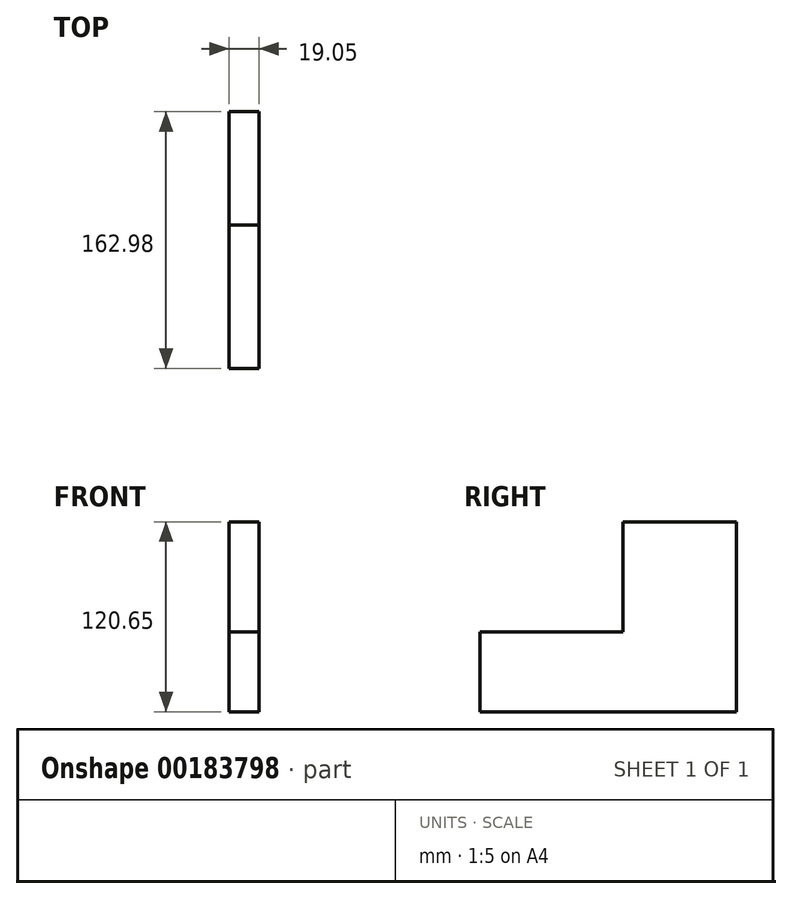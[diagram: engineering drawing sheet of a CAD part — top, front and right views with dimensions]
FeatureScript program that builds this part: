
annotation { "Feature Type Name" : "Feature", "Feature Type Description" : "" }
export const myFeature = defineFeature(function(context is Context, id is Id, definition is map)
    precondition{}
    {
        {
            var Q0;
            Q0=qCreatedBy(makeId("Right.planeOp"),FACE);
            var sketch = newSketch(context, id + "F0", { "sketchPlane" : qUnion([Q0])});
            skLineSegment(sketch, "E0.bottom", {"start": v(0, 0) * mm, "end": v(273.05, 0) * mm});
            skLineSegment(sketch, "E0.top", {"start": v(0, 228.6) * mm, "end": v(273.05, 228.6) * mm});
            skLineSegment(sketch, "E0.left", {"start": v(0, 0) * mm, "end": v(0, 228.6) * mm});
            skLineSegment(sketch, "E0.right", {"start": v(273.05, 0) * mm, "end": v(273.05, 228.6) * mm});
            skSolve(sketch);
        }
        {
            var Q0;
            Q0=qSketchRegion(id+"F0",true);
            extrude(context, id + "F1", {"entities" : qUnion([Q0]), "oppositeDirection" : true, "depth" : 19.05 * mm});
        }
        {
            var Q0;
            Q0=makeQuery(id+"F1.opExtrude","CAP_FACE",FACE,{"disambiguationData":[OSD([sQuery(id+"F0.wireOp",EDGE,"E0.bottom"),sQuery(id+"F0.wireOp",EDGE,"E0.top"),sQuery(id+"F0.wireOp",EDGE,"E0.left"),sQuery(id+"F0.wireOp",EDGE,"E0.right")])],"isStart":true});
            var sketch = newSketch(context, id + "F2", { "sketchPlane" : qUnion([Q0])});
            skLineSegment(sketch, "E1", {"start": v(91.02, 228.6) * mm, "end": v(91.02, 69.85) * mm, "construction": true});
            skLineSegment(sketch, "E2", {"start": v(182.03, 228.6) * mm, "end": v(182.03, 139.7) * mm, "construction": true});
            skLineSegment(sketch, "E3", {"start": v(0, 190.24) * mm, "end": v(91.02, 190.24) * mm, "construction": true});
            skLineSegment(sketch, "E4", {"start": v(91.02, 190.24) * mm, "end": v(182.03, 190.24) * mm, "construction": true});
            skLineSegment(sketch, "E5", {"start": v(182.03, 190.24) * mm, "end": v(273.05, 190.24) * mm, "construction": true});
            skLineSegment(sketch, "E6", {"start": v(273.05, 139.7) * mm, "end": v(182.03, 139.7) * mm});
            skLineSegment(sketch, "E7", {"start": v(273.05, 69.85) * mm, "end": v(91.02, 69.85) * mm});
            skLineSegment(sketch, "E8", {"start": v(40.37, 139.7) * mm, "end": v(40.37, 69.85) * mm, "construction": true});
            skLineSegment(sketch, "E9", {"start": v(40.37, 69.85) * mm, "end": v(40.37, 0) * mm, "construction": true});
            skLineSegment(sketch, "E10", {"start": v(91.02, 69.85) * mm, "end": v(91.02, 0) * mm});
            skLineSegment(sketch, "E11", {"start": v(91.02, 69.85) * mm, "end": v(0, 69.85) * mm, "construction": true});
            skLineSegment(sketch, "E12", {"start": v(182.03, 139.7) * mm, "end": v(182.03, 0) * mm});
            skLineSegment(sketch, "E13", {"start": v(182.03, 139.7) * mm, "end": v(0, 139.7) * mm, "construction": true});
            skSolve(sketch);
        }
        {
            var Q0;
            {var subQ1=sQuery(id+"F2.wireOp",EDGE,"E6");Q0=makeQuery(id+"F2.imprint","IMPRINT",FACE,{"disambiguationData":[TD([[makeQuery(id+"F2.imprint","IMPRINT",EDGE,{"derivedFrom":subQ1}),-1.0]])]});}
            var Q1;
            Q1=makeQuery(id+"F1.opExtrude","CAP_FACE",FACE,{"disambiguationData":[OSD([sQuery(id+"F0.wireOp",EDGE,"E0.bottom"),sQuery(id+"F0.wireOp",EDGE,"E0.top"),sQuery(id+"F0.wireOp",EDGE,"E0.left"),sQuery(id+"F0.wireOp",EDGE,"E0.right")])],"isStart":false});
            extrude(context, id + "F3", {"entities" : qUnion([Q0]), "operationType" : NewBodyOperationType.REMOVE, "endBound" : BoundingType.UP_TO_SURFACE, "oppositeDirection" : true, "endBoundEntityFace" : qUnion([Q1]), "depth" : 25.4 * mm});
        }
        {
            var Q0;
            Q0=makeQuery(id+"F1.opExtrude","CAP_FACE",FACE,{"disambiguationData":[OSD([sQuery(id+"F0.wireOp",EDGE,"E0.bottom"),sQuery(id+"F0.wireOp",EDGE,"E0.top"),sQuery(id+"F0.wireOp",EDGE,"E0.left"),sQuery(id+"F0.wireOp",EDGE,"E0.right")])],"isStart":true});
            var sketch = newSketch(context, id + "F4", { "sketchPlane" : qUnion([Q0])});
            skLineSegment(sketch, "E14.0", {"start": v(110.07, 50.8) * mm, "end": v(110.07, 0) * mm});
            skLineSegment(sketch, "E14.1", {"start": v(201.08, 50.8) * mm, "end": v(110.07, 50.8) * mm});
            skLineSegment(sketch, "E14.2", {"start": v(201.08, 120.65) * mm, "end": v(201.08, 50.8) * mm});
            skLineSegment(sketch, "E14.3", {"start": v(273.05, 120.65) * mm, "end": v(201.08, 120.65) * mm});
            skSolve(sketch);
        }
        {
            var Q0;
            {var subQ3=sQuery(id+"F4.wireOp",EDGE,"E14.0");Q0=makeQuery(id+"F4.imprint","IMPRINT",FACE,{"disambiguationData":[TD([[makeQuery(id+"F4.imprint","IMPRINT",EDGE,{"derivedFrom":subQ3}),-1.0]])]});}
            var Q1;
            Q1=makeQuery(id+"F1.opExtrude","CAP_FACE",FACE,{"disambiguationData":[OSD([sQuery(id+"F0.wireOp",EDGE,"E0.bottom"),sQuery(id+"F0.wireOp",EDGE,"E0.top"),sQuery(id+"F0.wireOp",EDGE,"E0.left"),sQuery(id+"F0.wireOp",EDGE,"E0.right")])],"isStart":false});
            extrude(context, id + "F5", {"entities" : qUnion([Q0]), "operationType" : NewBodyOperationType.REMOVE, "endBound" : BoundingType.UP_TO_SURFACE, "oppositeDirection" : true, "endBoundEntityFace" : qUnion([Q1]), "depth" : 25.4 * mm});
        }
    });
